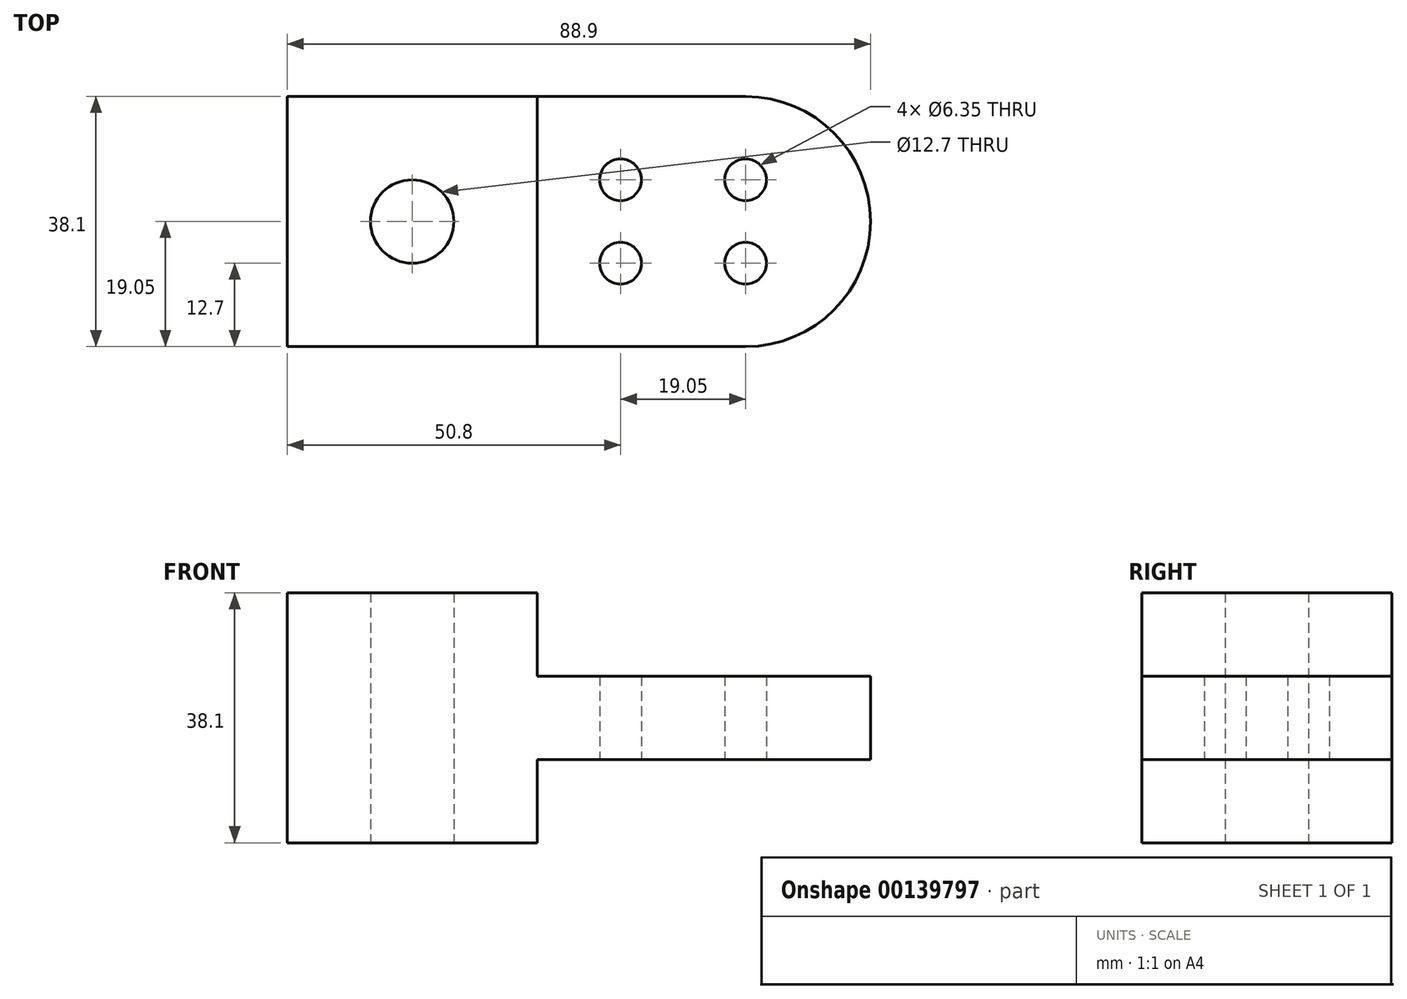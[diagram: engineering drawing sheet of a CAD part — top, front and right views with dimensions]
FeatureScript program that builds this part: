
annotation { "Feature Type Name" : "Feature", "Feature Type Description" : "" }
export const myFeature = defineFeature(function(context is Context, id is Id, definition is map)
    precondition{}
    {
        {
            var Q0;
            Q0=qCreatedBy(makeId("Top.planeOp"),FACE);
            var sketch = newSketch(context, id + "F0", { "sketchPlane" : qUnion([Q0])});
            skLineSegment(sketch, "E0.bottom", {"start": v(0, 0) * mm, "end": v(38.1, 0) * mm});
            skLineSegment(sketch, "E0.top", {"start": v(0, 38.1) * mm, "end": v(38.1, 38.1) * mm});
            skLineSegment(sketch, "E0.left", {"start": v(0, 0) * mm, "end": v(0, 38.1) * mm});
            skLineSegment(sketch, "E0.right", {"start": v(38.1, 0) * mm, "end": v(38.1, 38.1) * mm});
            skLineSegment(sketch, "E1.bottom", {"start": v(38.1, 0) * mm, "end": v(69.85, 0) * mm});
            skLineSegment(sketch, "E1.top", {"start": v(38.1, 38.1) * mm, "end": v(69.85, 38.1) * mm});
            skArc(sketch, "E2", {"start": v(69.85, 0) * mm, "mid": v(88.9, 19.05) * mm, "end": v(69.85, 38.1) * mm});
            skCircle(sketch, "E3", {"center": v(19.05, 19.05) * mm, "radius": 6.35 * mm});
            skLineSegment(sketch, "E4", {"start": v(50.8, 35.41) * mm, "end": v(50.8, 0.6) * mm, "construction": true});
            skLineSegment(sketch, "E5", {"start": v(69.85, 38.1) * mm, "end": v(69.85, 0) * mm, "construction": true});
            skLineSegment(sketch, "E6", {"start": v(43.33, 25.4) * mm, "end": v(77.13, 25.4) * mm, "construction": true});
            skLineSegment(sketch, "E7", {"start": v(42.47, 12.7) * mm, "end": v(75.56, 12.7) * mm, "construction": true});
            skCircle(sketch, "E8", {"center": v(50.8, 25.4) * mm, "radius": 3.18 * mm});
            skCircle(sketch, "E9", {"center": v(69.85, 25.4) * mm, "radius": 3.18 * mm});
            skCircle(sketch, "E10", {"center": v(69.85, 12.7) * mm, "radius": 3.18 * mm});
            skCircle(sketch, "E11", {"center": v(50.8, 12.7) * mm, "radius": 3.18 * mm});
            skSolve(sketch);
        }
        {
            var Q0;
            Q0=makeQuery(id+"F0.imprint","IMPRINT",FACE,{"disambiguationData":[TD([[makeQuery(id+"F0.imprint","IMPRINT",EDGE,{"derivedFrom":sQuery(id+"F0.wireOp",EDGE,"E0.bottom")}),1.0]])]});
            extrude(context, id + "F1", {"entities" : qUnion([Q0]), "endBound" : BoundingType.SYMMETRIC, "depth" : 38.1 * mm});
        }
        {
            var Q0;
            Q0=makeQuery(id+"F0.imprint","IMPRINT",FACE,{"disambiguationData":[TD([[makeQuery(id+"F0.imprint","IMPRINT",EDGE,{"derivedFrom":sQuery(id+"F0.wireOp",EDGE,"E1.bottom")}),1.0]])]});
            extrude(context, id + "F2", {"entities" : qUnion([Q0]), "operationType" : NewBodyOperationType.ADD, "endBound" : BoundingType.SYMMETRIC, "depth" : 12.7 * mm});
        }
    });
